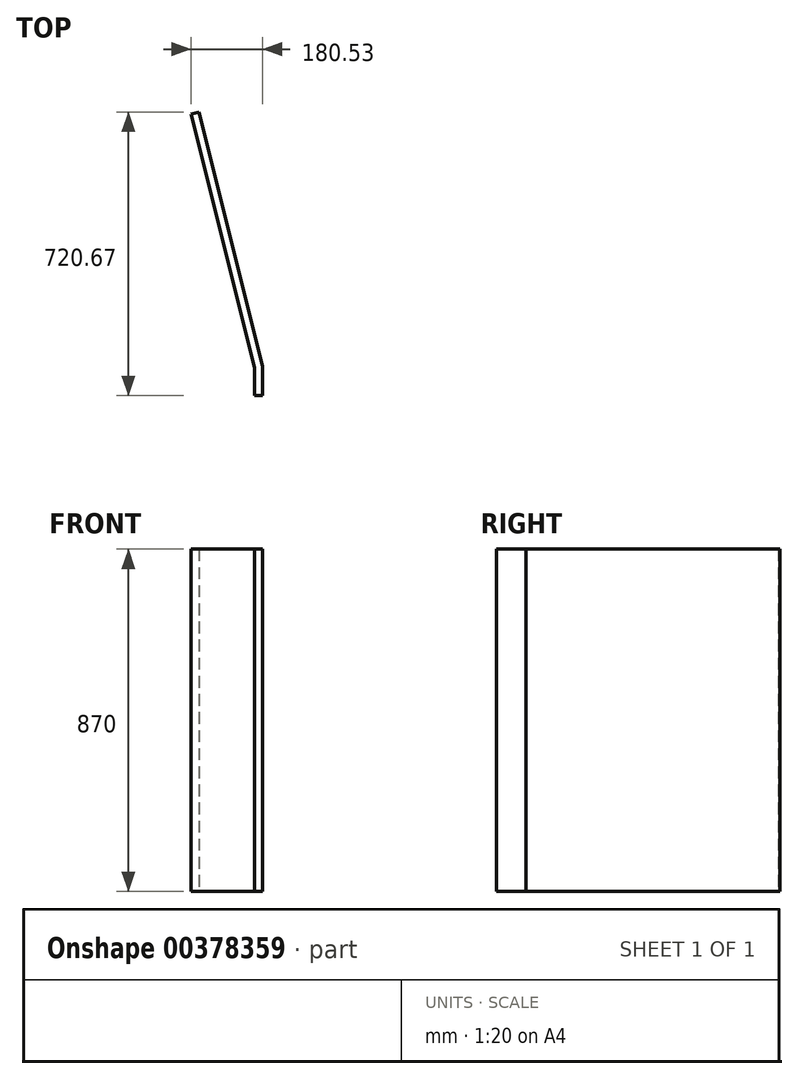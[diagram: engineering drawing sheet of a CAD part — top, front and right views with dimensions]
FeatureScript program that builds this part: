
annotation { "Feature Type Name" : "Feature", "Feature Type Description" : "" }
export const myFeature = defineFeature(function(context is Context, id is Id, definition is map)
    precondition{}
    {
        {
            var Q0;
            Q0=qCreatedBy(makeId("Top.planeOp"),FACE);
            var sketch = newSketch(context, id + "F0", { "sketchPlane" : qUnion([Q0])});
            skLineSegment(sketch, "E0.top", {"start": v(10, -37.23) * mm, "end": v(-10, -37.23) * mm});
            skLineSegment(sketch, "E0.left", {"start": v(10, 37.23) * mm, "end": v(10, -37.23) * mm});
            skLineSegment(sketch, "E0.right", {"start": v(-10, 34.77) * mm, "end": v(-10, -37.23) * mm});
            skPoint(sketch, "E0.middle", {"position": v(0, 0) * mm});
            skLineSegment(sketch, "E1", {"start": v(10, 37.23) * mm, "end": v(-10, 34.77) * mm});
            skLineSegment(sketch, "E2", {"start": v(10, 37.23) * mm, "end": v(-151.12, 683.44) * mm});
            skLineSegment(sketch, "E3", {"start": v(-151.12, 683.44) * mm, "end": v(-170.53, 678.6) * mm});
            skLineSegment(sketch, "E4", {"start": v(-170.53, 678.6) * mm, "end": v(-10, 34.77) * mm});
            skSolve(sketch);
        }
        {
            var Q0;
            Q0 = qSketchRegion(id + "F0", true);
            extrude(context, id + "F1", {"entities" : qUnion([Q0]), "depth" : 870 * mm});
        }
    });
